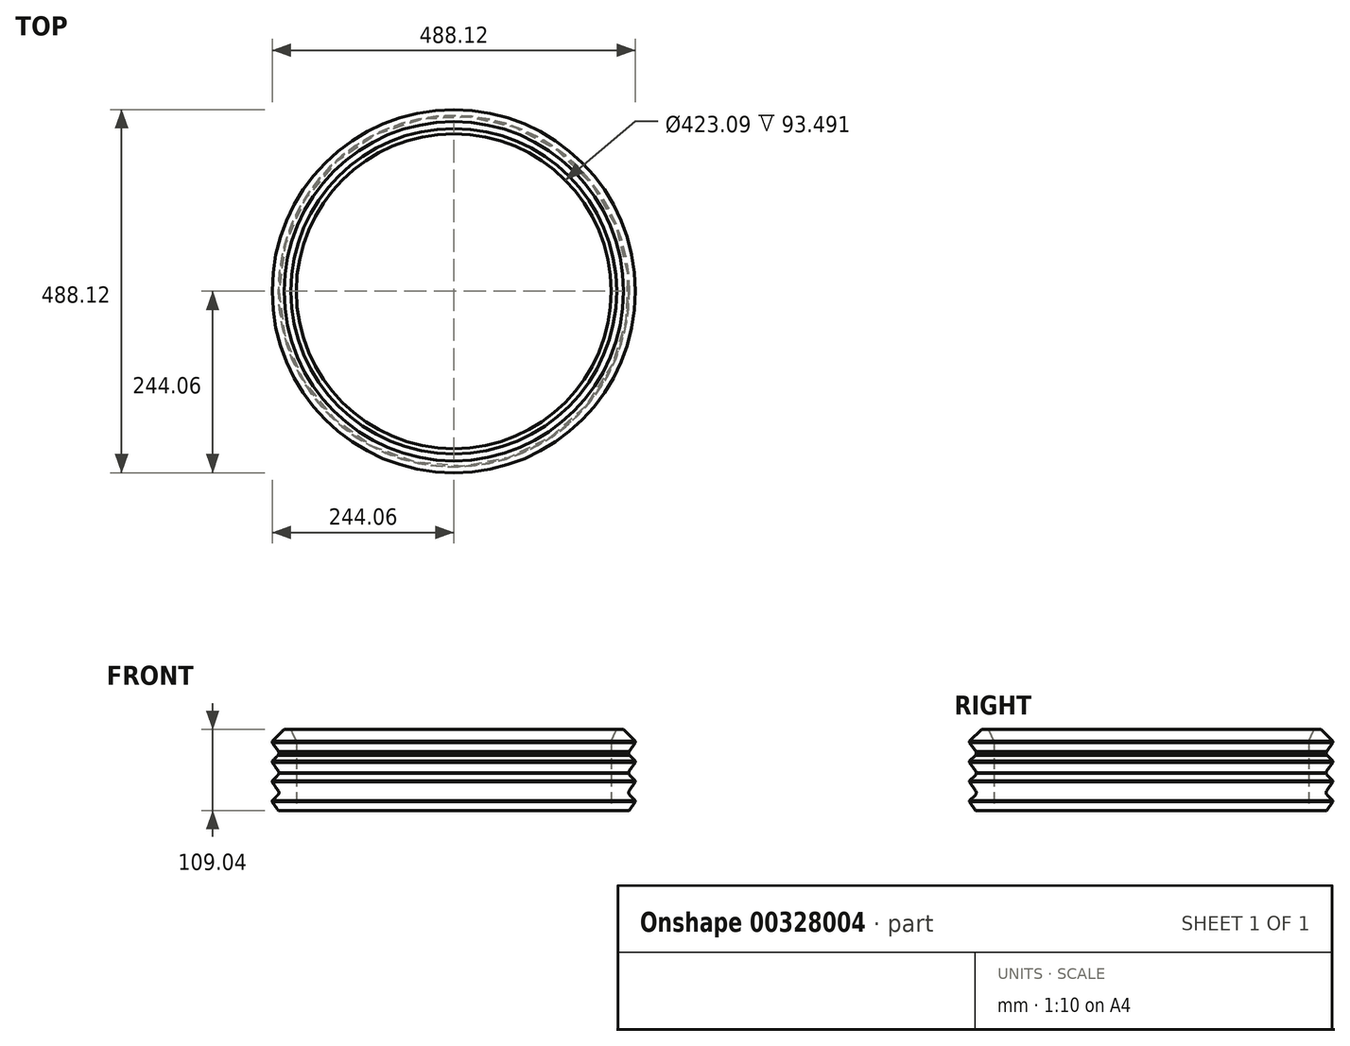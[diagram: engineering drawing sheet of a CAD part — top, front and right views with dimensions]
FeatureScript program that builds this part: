
annotation { "Feature Type Name" : "Feature", "Feature Type Description" : "" }
export const myFeature = defineFeature(function(context is Context, id is Id, definition is map)
    precondition{}
    {
        {
            var Q0;
            Q0=qCreatedBy(makeId("Front.planeOp"),FACE);
            var sketch = newSketch(context, id + "F0", { "sketchPlane" : qUnion([Q0])});
            skPoint(sketch, "E0.MirrorP", {"position": v(235.84, 0) * mm});
            skLineSegment(sketch, "E1.MirrorCS", {"start": v(211.54, 0) * mm, "end": v(211.54, 93.5) * mm});
            skLineSegment(sketch, "E2.MirrorCS", {"start": v(211.54, 0) * mm, "end": v(235.84, 0) * mm});
            skLineSegment(sketch, "E3.MirrorCS", {"start": v(218.8, 109.04) * mm, "end": v(228.03, 109.04) * mm});
            skLineSegment(sketch, "E4.MirrorCS", {"start": v(244.06, 93.02) * mm, "end": v(244.06, 91.47) * mm});
            skLineSegment(sketch, "E5.MirrorCS", {"start": v(244.06, 92.99) * mm, "end": v(244.06, 91.47) * mm});
            skLineSegment(sketch, "E6", {"start": v(235.84, 0) * mm, "end": v(244.06, 11.73) * mm});
            skLineSegment(sketch, "E7", {"start": v(244.06, 13.26) * mm, "end": v(236.31, 21) * mm});
            skLineSegment(sketch, "E8", {"start": v(244.06, 38.28) * mm, "end": v(235.83, 26.53) * mm});
            skLineSegment(sketch, "E9", {"start": v(235.04, 50.92) * mm, "end": v(235.04, 50.32) * mm});
            skLineSegment(sketch, "E10", {"start": v(244.06, 39.8) * mm, "end": v(236.3, 47.56) * mm});
            skLineSegment(sketch, "E11", {"start": v(244.06, 64.87) * mm, "end": v(235.8, 53.1) * mm});
            skLineSegment(sketch, "E12", {"start": v(244.06, 66.4) * mm, "end": v(236.14, 74.3) * mm});
            skLineSegment(sketch, "E13", {"start": v(244.06, 91.47) * mm, "end": v(235.69, 79.52) * mm});
            skLineSegment(sketch, "E14", {"start": v(235.04, 76.85) * mm, "end": v(235.04, 77.58) * mm});
            skLineSegment(sketch, "E15", {"start": v(244.06, 92.99) * mm, "end": v(243.17, 93.87) * mm});
            skLineSegment(sketch, "E16.0", {"start": v(244.07, 93) * mm, "end": v(228.03, 109.04) * mm});
            skLineSegment(sketch, "E17.trimOffspring", {"start": v(244.06, 13.26) * mm, "end": v(244.06, 11.73) * mm});
            skLineSegment(sketch, "E18.trimOffspring", {"start": v(244.06, 39.8) * mm, "end": v(244.06, 38.28) * mm});
            skLineSegment(sketch, "E19.trimOffspring", {"start": v(244.06, 66.4) * mm, "end": v(244.06, 64.87) * mm});
            skArc(sketch, "E20", {"start": v(235.83, 26.53) * mm, "mid": v(235.07, 23.68) * mm, "end": v(236.31, 21) * mm});
            skLineSegment(sketch, "E21", {"start": v(218.8, 109.04) * mm, "end": v(211.54, 93.5) * mm});
            skLineSegment(sketch, "E22", {"start": v(0, 0) * mm, "end": v(0, 28.33) * mm});
            skLineSegment(sketch, "E23", {"start": v(239.35, 77.21) * mm, "end": v(235.93, 79.86) * mm});
            skArc(sketch, "E24", {"start": v(235.93, 79.86) * mm, "mid": v(235.04, 76.83) * mm, "end": v(236.44, 74) * mm});
            skLineSegment(sketch, "E25", {"start": v(239.35, 50.62) * mm, "end": v(235.8, 53.1) * mm});
            skArc(sketch, "E26", {"start": v(235.8, 53.1) * mm, "mid": v(235.04, 50.24) * mm, "end": v(236.3, 47.56) * mm});
            skSolve(sketch);
        }
        {
            var Q0;
            Q0 = qSketchRegion(id + "F0", true);
            var Q1;
            Q1=sQuery(id+"F0.wireOp",EDGE,"E22");
            revolve(context, id + "F1", {"entities" : qUnion([Q0]), "axis" : qUnion([Q1]), "revolveType" : RevolveType.FULL});
        }
    });
